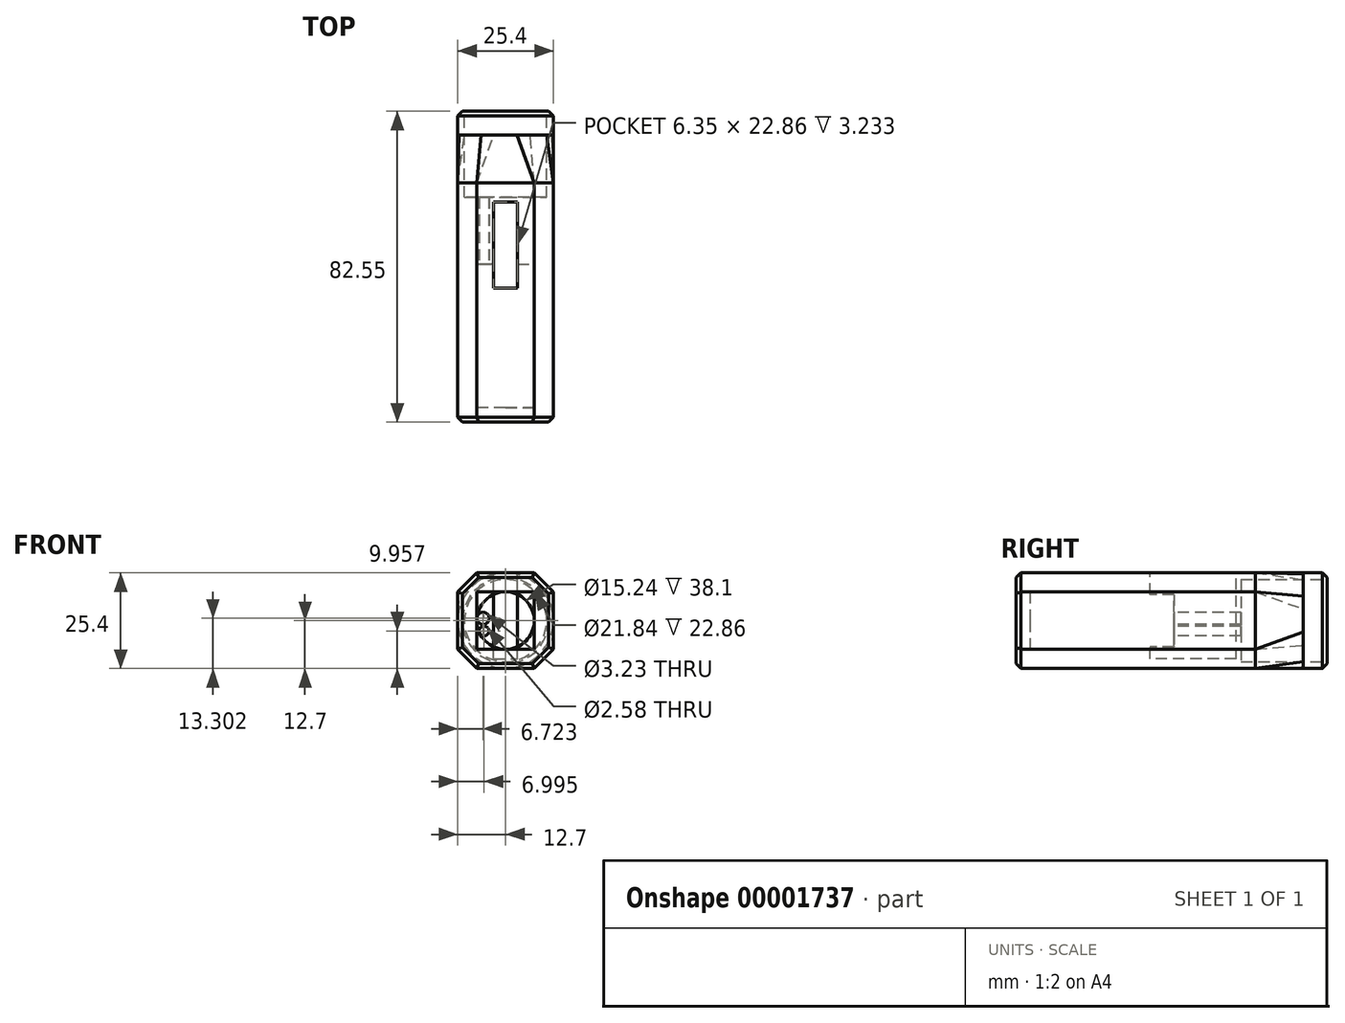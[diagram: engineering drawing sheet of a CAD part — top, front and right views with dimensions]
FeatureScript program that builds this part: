
annotation { "Feature Type Name" : "Feature", "Feature Type Description" : "" }
export const myFeature = defineFeature(function(context is Context, id is Id, definition is map)
    precondition{}
    {
        {
            var Q0;
            Q0=qCreatedBy(makeId("Front.planeOp"),FACE);
            var sketch = newSketch(context, id + "F0", { "sketchPlane" : qUnion([Q0])});
            skLineSegment(sketch, "E0.bottom", {"start": v(0, 0) * mm, "end": v(-25.4, 0) * mm});
            skLineSegment(sketch, "E0.top", {"start": v(0, 25.4) * mm, "end": v(-25.4, 25.4) * mm});
            skLineSegment(sketch, "E0.left", {"start": v(0, 0) * mm, "end": v(0, 25.4) * mm});
            skLineSegment(sketch, "E0.right", {"start": v(-25.4, 0) * mm, "end": v(-25.4, 25.4) * mm});
            skSolve(sketch);
        }
        {
            var Q0;
            Q0 = qSketchRegion(id + "F0", true);
            extrude(context, id + "F1", {"entities" : qUnion([Q0]), "depth" : 63.5 * mm});
        }
        {
            var Q0;
            Q0=makeQuery(id+"F1.opExtrude","CAP_FACE",FACE,{"disambiguationData":[OSD([sQuery(id+"F0.wireOp",EDGE,"E0.bottom"),sQuery(id+"F0.wireOp",EDGE,"E0.top"),sQuery(id+"F0.wireOp",EDGE,"E0.left"),sQuery(id+"F0.wireOp",EDGE,"E0.right")])],"isStart":false});
            var sketch = newSketch(context, id + "F2", { "sketchPlane" : qUnion([Q0])});
            skLineSegment(sketch, "E1.rect.bottom", {"start": v(-5.08, 5.08) * mm, "end": v(-20.32, 5.08) * mm});
            skLineSegment(sketch, "E1.rect.top", {"start": v(-5.08, 20.32) * mm, "end": v(-20.32, 20.32) * mm});
            skLineSegment(sketch, "E1.rect.left", {"start": v(-5.08, 5.08) * mm, "end": v(-5.08, 20.32) * mm});
            skLineSegment(sketch, "E1.rect.right", {"start": v(-20.32, 5.08) * mm, "end": v(-20.32, 20.32) * mm});
            skPoint(sketch, "E1.rect.middle", {"position": v(-12.7, 12.7) * mm});
            skPoint(sketch, "E1.rect.middle.positionSnap0", {"position": v(-25.4, 12.7) * mm});
            skPoint(sketch, "E1.rect.middle.positionSnap1", {"position": v(-12.7, 25.4) * mm});
            skPoint(sketch, "E1.rect.centerSnap0", {"position": v(-25.4, 12.7) * mm});
            skPoint(sketch, "E1.rect.centerSnap1", {"position": v(-12.7, 25.4) * mm});
            skSolve(sketch);
        }
        {
            var Q0;
            Q0=makeQuery(id+"F2.imprint","IMPRINT",FACE,{"disambiguationData":[TD([[makeQuery(id+"F2.imprint","IMPRINT",EDGE,{"derivedFrom":sQuery(id+"F2.wireOp",EDGE,"E1.rect.bottom")}),-1.0]])]});
            extrude(context, id + "F3", {"entities" : qUnion([Q0]), "operationType" : NewBodyOperationType.REMOVE, "oppositeDirection" : true, "depth" : 3.8 * mm});
        }
        {
            var Q0;
            Q0=makeQuery(id+"F3.boolean.opBoolean","COPY",FACE,{"derivedFrom":makeQuery(id+"F3.opExtrude","CAP_FACE",FACE,{"disambiguationData":[OSD([sQuery(id+"F2.wireOp",EDGE,"E1.rect.bottom"),sQuery(id+"F2.wireOp",EDGE,"E1.rect.top"),sQuery(id+"F2.wireOp",EDGE,"E1.rect.left"),sQuery(id+"F2.wireOp",EDGE,"E1.rect.right")])],"isStart":false})});
            var sketch = newSketch(context, id + "F4", { "sketchPlane" : qUnion([Q0])});
            skCircle(sketch, "E2", {"center": v(-12.7, 12.7) * mm, "radius": 7.62 * mm});
            skPoint(sketch, "E2.centerSnap0", {"position": v(-12.7, 5.08) * mm});
            skPoint(sketch, "E2.centerSnap1", {"position": v(-20.32, 12.7) * mm});
            skSolve(sketch);
        }
        {
            var Q0;
            Q0=makeQuery(id+"F4.imprint","IMPRINT",FACE,{"disambiguationData":[TD([[makeQuery(id+"F4.imprint","IMPRINT",EDGE,{"derivedFrom":sQuery(id+"F4.wireOp",EDGE,"E2")}),1.0]])]});
            extrude(context, id + "F5", {"entities" : qUnion([Q0]), "operationType" : NewBodyOperationType.REMOVE, "oppositeDirection" : true, "depth" : 38.1 * mm});
        }
        {
            var Q0;
            Q0=makeQuery(id+"F1.opExtrude","SWEPT_FACE",FACE,{"disambiguationData":[OSD([sQuery(id+"F0.wireOp",EDGE,"E0.top")])]});
            var sketch = newSketch(context, id + "F6", { "sketchPlane" : qUnion([Q0])});
            skLineSegment(sketch, "E3", {"start": v(-12.7, 0) * mm, "end": v(-12.7, -16.51) * mm, "construction": true});
            skSolve(sketch);
        }
        {
            var Q0;
            {var subQ0=sQuery(id+"F0.wireOp",EDGE,"E0.top");Q0=makeQuery(id+"F6.imprint","IMPRINT",FACE,{"disambiguationData":[TD([[makeQuery(id+"F6.imprint","IMPRINT",EDGE,{"derivedFrom":makeQuery(id+"F1.opExtrude","CAP_EDGE",EDGE,{"disambiguationData":[OSD([subQ0])],"isStart":true})}),1.0]])]});}
            var sketch = newSketch(context, id + "F7", { "sketchPlane" : qUnion([Q0])});
            skLineSegment(sketch, "E4.rect.bottom", {"start": v(-15.88, -5.08) * mm, "end": v(-9.53, -5.08) * mm});
            skLineSegment(sketch, "E4.rect.top", {"start": v(-15.88, -27.94) * mm, "end": v(-9.53, -27.94) * mm});
            skLineSegment(sketch, "E4.rect.left", {"start": v(-15.88, -5.08) * mm, "end": v(-15.88, -27.94) * mm});
            skLineSegment(sketch, "E4.rect.right", {"start": v(-9.53, -5.08) * mm, "end": v(-9.53, -27.94) * mm});
            skPoint(sketch, "E4.rect.middle", {"position": v(-12.7, -16.51) * mm});
            skSolve(sketch);
        }
        {
            var Q0;
            Q0=makeQuery(id+"F7.imprint","IMPRINT",FACE,{"disambiguationData":[TD([[makeQuery(id+"F7.imprint","IMPRINT",EDGE,{"derivedFrom":sQuery(id+"F7.wireOp",EDGE,"E4.rect.bottom")}),-1.0]])]});
            extrude(context, id + "F8", {"entities" : qUnion([Q0]), "operationType" : NewBodyOperationType.REMOVE, "oppositeDirection" : true, "depth" : 22.86 * mm});
        }
        {
            var Q0;
            Q0=makeQuery(id+"F1.opExtrude","SWEPT_EDGE",EDGE,{"disambiguationData":[OSD([sQuery(id+"F0.wireOp",EDGE,"E0.top"),sQuery(id+"F0.wireOp",EDGE,"E0.left")])]});
            var Q1;
            Q1=makeQuery(id+"F1.opExtrude","SWEPT_EDGE",EDGE,{"disambiguationData":[OSD([sQuery(id+"F0.wireOp",EDGE,"E0.top"),sQuery(id+"F0.wireOp",EDGE,"E0.right")])]});
            var Q2;
            Q2=makeQuery(id+"F1.opExtrude","SWEPT_EDGE",EDGE,{"disambiguationData":[OSD([sQuery(id+"F0.wireOp",EDGE,"E0.bottom"),sQuery(id+"F0.wireOp",EDGE,"E0.right")])]});
            var Q3;
            Q3=makeQuery(id+"F1.opExtrude","SWEPT_EDGE",EDGE,{"disambiguationData":[OSD([sQuery(id+"F0.wireOp",EDGE,"E0.bottom"),sQuery(id+"F0.wireOp",EDGE,"E0.left")])]});
            chamfer(context, id + "F9", {"entities" : qUnion([Q0, Q1, Q2, Q3]), "width" : 5.08 * mm, "tangentPropagation" : true});
        }
        {
            var Q0;
            Q0=qCreatedBy(makeId("Front.planeOp"),FACE);
            cPlane(context, id + "F10", {"entities" : qUnion([Q0]), "cplaneType" : CPlaneType.OFFSET, "offset" : 12.7 * mm, "oppositeDirection" : true, "width" : 152.4 * mm, "height" : 152.4 * mm});
        }
        {
            var Q0;
            Q0=qCreatedBy(id+"F10.planeOp",FACE);
            var sketch = newSketch(context, id + "F11", { "sketchPlane" : qUnion([Q0])});
            skLineSegment(sketch, "E5", {"start": v(0, 0) * mm, "end": v(-12.7, 0) * mm, "construction": true});
            skLineSegment(sketch, "E6", {"start": v(-12.7, 0) * mm, "end": v(-12.7, 12.7) * mm, "construction": true});
            skSolve(sketch);
        }
        {
            var Q0;
            Q0=qCreatedBy(id+"F10.planeOp",FACE);
            var sketch = newSketch(context, id + "F12", { "sketchPlane" : qUnion([Q0])});
            skCircle(sketch, "E7", {"center": v(-12.7, 12.7) * mm, "radius": 12.7 * mm});
            skSolve(sketch);
        }
        {
            var Q1;
            Q1=makeQuery(id+"F1.opExtrude","CAP_FACE",FACE,{"disambiguationData":[OSD([sQuery(id+"F0.wireOp",EDGE,"E0.bottom"),sQuery(id+"F0.wireOp",EDGE,"E0.top"),sQuery(id+"F0.wireOp",EDGE,"E0.left"),sQuery(id+"F0.wireOp",EDGE,"E0.right")])],"isStart":true});
            var Q2;
            Q2=makeQuery(id+"F12.imprint","IMPRINT",FACE,{"disambiguationData":[TD([[makeQuery(id+"F12.imprint","IMPRINT",EDGE,{"derivedFrom":sQuery(id+"F12.wireOp",EDGE,"E7")}),1.0]])]});
            loft(context, id + "F13", {"operationType" : NewBodyOperationType.ADD, "sheetProfilesArray" : [{ "sheetProfileEntities" : qUnion([Q1]) }, { "sheetProfileEntities" : qUnion([Q2]) }]});
        }
        {
            var Q0;
            Q0=makeQuery(id+"F13.opLoft","CAP_FACE",FACE,{"disambiguationData":[OSD([makeQuery(id+"F12.imprint","IMPRINT",FACE,{"disambiguationData":[TD([[makeQuery(id+"F12.imprint","IMPRINT",EDGE,{"derivedFrom":sQuery(id+"F12.wireOp",EDGE,"E7")}),1.0]])]})])],"isStart":true});
            extrude(context, id + "F14", {"entities" : qUnion([Q0]), "operationType" : NewBodyOperationType.ADD, "depth" : 6.35 * mm});
        }
        {
            var Q0;
            Q0=makeQuery(id+"F14.opExtrude","CAP_FACE",FACE,{"disambiguationData":[OSD([makeQuery(id+"F12.imprint","IMPRINT",FACE,{"disambiguationData":[TD([[makeQuery(id+"F12.imprint","IMPRINT",EDGE,{"derivedFrom":sQuery(id+"F12.wireOp",EDGE,"E7")}),1.0]])]})])],"isStart":false});
            var sketch = newSketch(context, id + "F15", { "sketchPlane" : qUnion([Q0])});
            skCircle(sketch, "E8", {"center": v(12.7, 12.7) * mm, "radius": 10.92 * mm});
            skSolve(sketch);
        }
        {
            var Q0;
            Q0=makeQuery(id+"F15.imprint","IMPRINT",FACE,{"disambiguationData":[TD([[makeQuery(id+"F15.imprint","IMPRINT",EDGE,{"derivedFrom":sQuery(id+"F15.wireOp",EDGE,"E8")}),1.0]])]});
            extrude(context, id + "F16", {"entities" : qUnion([Q0]), "operationType" : NewBodyOperationType.REMOVE, "oppositeDirection" : true, "depth" : 22.86 * mm});
        }
        {
            var Q0;
            {var subQ0=sQuery(id+"F4.wireOp",EDGE,"E2");Q0=makeQuery(id+"F8.boolean.opBoolean","SPLIT",FACE,{"disambiguationData":[TD([makeQuery(id+"F8.opExtrude","SWEPT_FACE",FACE,{"disambiguationData":[OSD([sQuery(id+"F7.wireOp",EDGE,"E4.rect.left")])]})])],"derivedFrom":makeQuery(id+"F5.boolean.opBoolean","COPY",FACE,{"derivedFrom":makeQuery(id+"F5.opExtrude","CAP_FACE",FACE,{"disambiguationData":[OSD([subQ0])],"isStart":false})})});}
            var sketch = newSketch(context, id + "F17", { "sketchPlane" : qUnion([Q0])});
            skCircle(sketch, "E9", {"center": v(-18.68, 13.3) * mm, "radius": 1.61 * mm});
            skSolve(sketch);
        }
        {
            var Q0;
            Q0 = qSketchRegion(id + "F17", true);
            extrude(context, id + "F18", {"entities" : qUnion([Q0]), "operationType" : NewBodyOperationType.REMOVE, "oppositeDirection" : true, "depth" : 25.4 * mm});
        }
        {
            var Q0;
            {var subQ0=sQuery(id+"F4.wireOp",EDGE,"E2");Q0=makeQuery(id+"F8.boolean.opBoolean","SPLIT",FACE,{"disambiguationData":[TD([makeQuery(id+"F8.opExtrude","SWEPT_FACE",FACE,{"disambiguationData":[OSD([sQuery(id+"F7.wireOp",EDGE,"E4.rect.left")])]})])],"derivedFrom":makeQuery(id+"F5.boolean.opBoolean","COPY",FACE,{"derivedFrom":makeQuery(id+"F5.opExtrude","CAP_FACE",FACE,{"disambiguationData":[OSD([subQ0])],"isStart":false})})});}
            var sketch = newSketch(context, id + "F19", { "sketchPlane" : qUnion([Q0])});
            skCircle(sketch, "E10", {"center": v(-18.4, 9.96) * mm, "radius": 1.29 * mm});
            skSolve(sketch);
        }
        {
            var Q0;
            Q0 = qSketchRegion(id + "F19", true);
            extrude(context, id + "F20", {"entities" : qUnion([Q0]), "operationType" : NewBodyOperationType.REMOVE, "oppositeDirection" : true, "depth" : 25.4 * mm});
        }
        {
            var Q0;
            {var subQ0=sQuery(id+"F12.wireOp",EDGE,"E7");var subQ1=sQuery(id+"F0.wireOp",EDGE,"E0.top");var subQ2=sQuery(id+"F0.wireOp",EDGE,"E0.right");var subQ3=sQuery(id+"F0.wireOp",EDGE,"E0.left");var subQ4=sQuery(id+"F0.wireOp",EDGE,"E0.bottom");var subQ5=makeQuery(id+"F1.opExtrude","CAP_FACE",FACE,{"disambiguationData":[OSD([subQ4,subQ1,subQ3,subQ2])],"isStart":true});var subQ6=makeQuery(id+"F1.opExtrude","SWEPT_EDGE",EDGE,{"disambiguationData":[OSD([subQ1,subQ3])]});Q0=makeQuery(id+"F14.opExtrude","CAP_EDGE",EDGE,{"disambiguationData":[OSD([subQ4,subQ1,subQ3,subQ2,subQ0]),TDD([makeQuery(id+"F13.opLoft","MID_CAP_EDGE",EDGE,{"disambiguationData":[OSD([subQ4,subQ1,subQ3,subQ2,subQ0]),TDD([makeQuery(id+"F9.opChamfer","BLEND_VERTEX",VERTEX,{"blendedFrom":[subQ6,subQ5,makeQuery(id+"F1.opExtrude","SWEPT_FACE",FACE,{"disambiguationData":[OSD([subQ3])]})],"blendedInto":[subQ5,makeQuery(id+"F1.opExtrude","SWEPT_FACE",FACE,{"disambiguationData":[OSD([subQ3])]})]}),makeQuery(id+"F9.opChamfer","BLEND_VERTEX",VERTEX,{"blendedFrom":[subQ6,subQ5,makeQuery(id+"F1.opExtrude","SWEPT_FACE",FACE,{"disambiguationData":[OSD([subQ1])]})],"blendedInto":[subQ5,makeQuery(id+"F1.opExtrude","SWEPT_FACE",FACE,{"disambiguationData":[OSD([subQ1])]})]}),makeQuery(id+"F12.imprint","IMPRINT",EDGE,{"derivedFrom":subQ0})])],"capPos":1.0})])],"isStart":false});}
            chamfer(context, id + "F21", {"entities" : qUnion([Q0]), "width" : 1.27 * mm, "tangentPropagation" : true});
        }
        {
            var Q0;
            Q0=makeQuery(id+"F1.opExtrude","CAP_EDGE",EDGE,{"disambiguationData":[OSD([sQuery(id+"F0.wireOp",EDGE,"E0.left")])],"isStart":false});
            var Q1;
            Q1=makeQuery(id+"F1.opExtrude","CAP_EDGE",EDGE,{"disambiguationData":[OSD([sQuery(id+"F0.wireOp",EDGE,"E0.bottom")])],"isStart":false});
            var Q2;
            Q2=makeQuery(id+"F1.opExtrude","CAP_EDGE",EDGE,{"disambiguationData":[OSD([sQuery(id+"F0.wireOp",EDGE,"E0.right")])],"isStart":false});
            var Q3;
            Q3=makeQuery(id+"F1.opExtrude","CAP_EDGE",EDGE,{"disambiguationData":[OSD([sQuery(id+"F0.wireOp",EDGE,"E0.top")])],"isStart":false});
            var Q4;
            {var subQ0=sQuery(id+"F0.wireOp",EDGE,"E0.left");var subQ1=sQuery(id+"F0.wireOp",EDGE,"E0.bottom");Q4=makeQuery(id+"F9.opChamfer","BLEND_EDGE",EDGE,{"blendedFrom":[makeQuery(id+"F1.opExtrude","SWEPT_EDGE",EDGE,{"disambiguationData":[OSD([subQ1,subQ0])]}),makeQuery(id+"F1.opExtrude","CAP_FACE",FACE,{"disambiguationData":[OSD([subQ1,sQuery(id+"F0.wireOp",EDGE,"E0.top"),subQ0,sQuery(id+"F0.wireOp",EDGE,"E0.right")])],"isStart":false})],"blendedInto":[makeQuery(id+"F1.opExtrude","CAP_FACE",FACE,{"disambiguationData":[OSD([subQ1,sQuery(id+"F0.wireOp",EDGE,"E0.top"),subQ0,sQuery(id+"F0.wireOp",EDGE,"E0.right")])],"isStart":false})]});}
            var Q5;
            {var subQ0=sQuery(id+"F0.wireOp",EDGE,"E0.left");var subQ1=sQuery(id+"F0.wireOp",EDGE,"E0.top");Q5=makeQuery(id+"F9.opChamfer","BLEND_EDGE",EDGE,{"blendedFrom":[makeQuery(id+"F1.opExtrude","SWEPT_EDGE",EDGE,{"disambiguationData":[OSD([subQ1,subQ0])]}),makeQuery(id+"F1.opExtrude","CAP_FACE",FACE,{"disambiguationData":[OSD([sQuery(id+"F0.wireOp",EDGE,"E0.bottom"),subQ1,subQ0,sQuery(id+"F0.wireOp",EDGE,"E0.right")])],"isStart":false})],"blendedInto":[makeQuery(id+"F1.opExtrude","CAP_FACE",FACE,{"disambiguationData":[OSD([sQuery(id+"F0.wireOp",EDGE,"E0.bottom"),subQ1,subQ0,sQuery(id+"F0.wireOp",EDGE,"E0.right")])],"isStart":false})]});}
            var Q6;
            {var subQ0=sQuery(id+"F0.wireOp",EDGE,"E0.right");var subQ1=sQuery(id+"F0.wireOp",EDGE,"E0.top");Q6=makeQuery(id+"F9.opChamfer","BLEND_EDGE",EDGE,{"blendedFrom":[makeQuery(id+"F1.opExtrude","SWEPT_EDGE",EDGE,{"disambiguationData":[OSD([subQ1,subQ0])]}),makeQuery(id+"F1.opExtrude","CAP_FACE",FACE,{"disambiguationData":[OSD([sQuery(id+"F0.wireOp",EDGE,"E0.bottom"),subQ1,sQuery(id+"F0.wireOp",EDGE,"E0.left"),subQ0])],"isStart":false})],"blendedInto":[makeQuery(id+"F1.opExtrude","CAP_FACE",FACE,{"disambiguationData":[OSD([sQuery(id+"F0.wireOp",EDGE,"E0.bottom"),subQ1,sQuery(id+"F0.wireOp",EDGE,"E0.left"),subQ0])],"isStart":false})]});}
            var Q7;
            {var subQ0=sQuery(id+"F0.wireOp",EDGE,"E0.right");var subQ1=sQuery(id+"F0.wireOp",EDGE,"E0.bottom");Q7=makeQuery(id+"F9.opChamfer","BLEND_EDGE",EDGE,{"blendedFrom":[makeQuery(id+"F1.opExtrude","SWEPT_EDGE",EDGE,{"disambiguationData":[OSD([subQ1,subQ0])]}),makeQuery(id+"F1.opExtrude","CAP_FACE",FACE,{"disambiguationData":[OSD([subQ1,sQuery(id+"F0.wireOp",EDGE,"E0.top"),sQuery(id+"F0.wireOp",EDGE,"E0.left"),subQ0])],"isStart":false})],"blendedInto":[makeQuery(id+"F1.opExtrude","CAP_FACE",FACE,{"disambiguationData":[OSD([subQ1,sQuery(id+"F0.wireOp",EDGE,"E0.top"),sQuery(id+"F0.wireOp",EDGE,"E0.left"),subQ0])],"isStart":false})]});}
            chamfer(context, id + "F22", {"entities" : qUnion([Q0, Q1, Q2, Q3, Q4, Q5, Q6, Q7]), "width" : 1.27 * mm, "tangentPropagation" : true});
        }
    });
